# Revit family: Base_Cabinet-Danver-Tall_Storage_Cabinets
name_source: partatom
category: Casework
units: mm (PartAtom-declared; Revit-internal decimal feet)

## family parameters
Always vertical = Yes
Classification Number = 23.40.35.17.47
Cut with Voids When Loaded = No
Room Calculation Point = No
Shared = No
Work Plane-Based = No

## types (1)
- Not a Type - Load Type Catalog
    C_Height = 7' - 7 1/2"
    Cabinet Material = Metal - Danver - Stainless Steel
    Construction Type = 304 Grade Stainless Steel
    Default Elevation = 0' - 0"
    Depth = 2' - 0"
    Depth+Door = 2' - 0 7/8"
    Description = Please Load Accompanying Type Catalog (txt.)
    Door Material = Metal - Danver - Stainless Steel
    Flat Drawer Material = Metal - Danver - Stainless Steel
    Full Door Count = 2
    Handle Material = Metal - Danver - Chrome Plated Steel
    Height = 8' - 0"
    Keynote = 12 35 28
    Manufacturer = Danver Outdoor Kitchens
    Model = Please Load Accompanying Type Catalog (txt.)
    Product Documentation Link = https://danver.com
    Product Name = Base Cabinet - Danver
    Product Page URL = https://danver.com
    Toe Height = 0' - 4 1/2"
    Toe Kick Material = Metal - Danver - Toe Kick
    Top Door Count = 2
    Top Door Height = 2' - 7 3/8"
    URL = www.danver.com
    V_Handle = No
    V_Lower Door1 = Yes
    V_Lower Door2 = Yes
    V_Top Door1 = Yes
    V_Top Door2 = Yes
    Version = 2019 - V1.0b
    Width = 2' - 0"

## geometry (parser evidence)
native form markers: Sweep x18
no freeform markers — native parametric forms only
